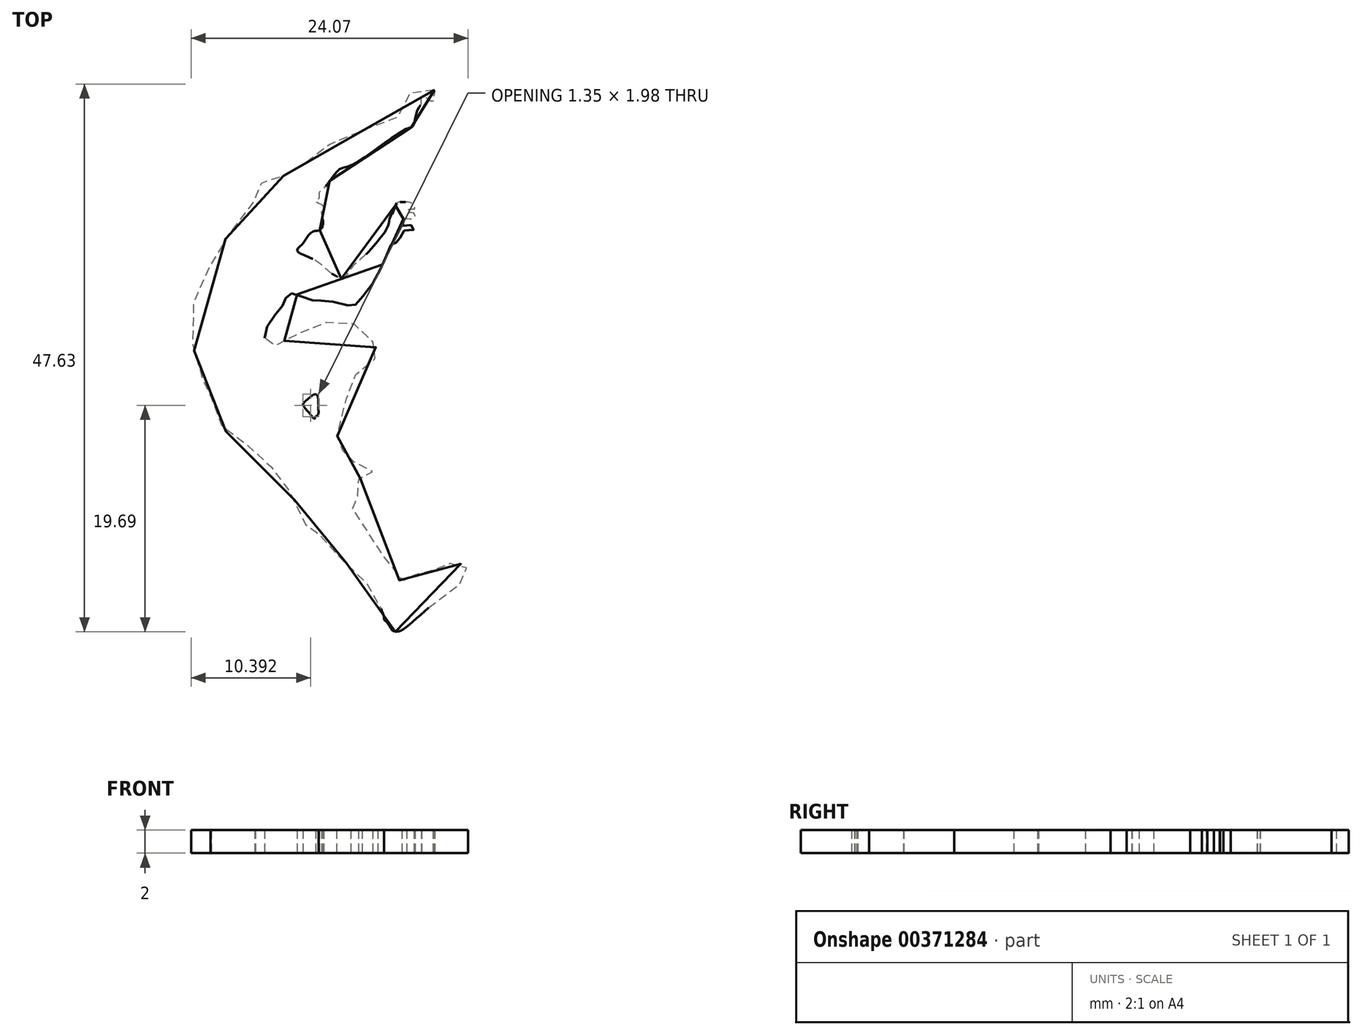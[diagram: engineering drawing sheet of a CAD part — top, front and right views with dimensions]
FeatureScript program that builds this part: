
annotation { "Feature Type Name" : "Feature", "Feature Type Description" : "" }
export const myFeature = defineFeature(function(context is Context, id is Id, definition is map)
    precondition{}
    {
        {
            var Q0;
            Q0=qCreatedBy(makeId("Top.planeOp"),FACE);
            var sketch = newSketch(context, id + "F0", { "sketchPlane" : qUnion([Q0])});
            skFitSpline(sketch, "E0", {"points": [v(-17.82, 62.19) * mm, v(-18.26, 62.6) * mm, v(-19.6, 62.47) * mm, v(-20.06, 61.56) * mm, v(-20.42, 60.89) * mm, v(-20.85, 59.9) * mm, v(-21.2, 59.78) * mm, v(-21.72, 59.64) * mm, v(-23.67, 58.82) * mm, v(-25.69, 58.05) * mm, v(-26.86, 57.47) * mm, v(-27.4, 57.23) * mm, v(-28.35, 56.34) * mm, v(-29.32, 55.6) * mm, v(-30.18, 55) * mm, v(-30.54, 55.02) * mm, v(-30.78, 54.76) * mm, v(-31.46, 54.78) * mm, v(-32.1, 54.54) * mm, v(-32.9, 54.04) * mm, v(-33.26, 53.31) * mm, v(-33.43, 52.83) * mm, v(-33.4, 52.47) * mm, v(-33.74, 52.4) * mm, v(-34.58, 51.13) * mm, v(-36.17, 48.94) * mm, v(-36.99, 47.42) * mm, v(-37.7, 46.25) * mm, v(-38.45, 44.66) * mm, v(-38.88, 43) * mm, v(-38.93, 40.93) * mm, v(-38.6, 39.18) * mm, v(-38.07, 37.76) * mm, v(-37.97, 36.9) * mm, v(-37.59, 35.98) * mm, v(-37.4, 35.64) * mm, v(-37.25, 35.62) * mm, v(-37.27, 34.95) * mm, v(-36.94, 34.06) * mm, v(-36.34, 33.02) * mm, v(-35.42, 31.97) * mm, v(-34.46, 31.46) * mm, v(-33.35, 30.88) * mm, v(-32.54, 29.83) * mm, v(-31.77, 29.18) * mm, v(-31.14, 28.14) * mm, v(-30.6, 27.52) * mm, v(-29.68, 25.9) * mm, v(-29.12, 24.6) * mm, v(-28.7, 24.06) * mm, v(-28.11, 24.03) * mm, v(-27.9, 24) * mm, v(-27.87, 23.7) * mm, v(-27.63, 23.17) * mm, v(-27.08, 22.45) * mm, v(-26.26, 21.75) * mm, v(-24.96, 20.55) * mm, v(-23.6, 19.18) * mm, v(-22.63, 17.95) * mm, v(-22.54, 17.3) * mm, v(-22.42, 16.94) * mm, v(-22.2, 16.34) * mm, v(-22.2, 16.12) * mm, v(-21.84, 15.76) * mm, v(-21.53, 15.26) * mm, v(-21.07, 15.06) * mm, v(-20.32, 15.42) * mm, v(-18.55, 16.96) * mm, v(-16.19, 18.8) * mm, v(-14.99, 19.78) * mm, v(-14.9, 20.16) * mm, v(-15.04, 20.62) * mm, v(-15.35, 20.9) * mm, v(-15.88, 21) * mm, v(-16.62, 20.93) * mm, v(-17.13, 20.55) * mm, v(-17.68, 20.47) * mm, v(-18.2, 20.23) * mm, v(-18.55, 19.94) * mm, v(-19.5, 20) * mm, v(-19.68, 19.75) * mm, v(-20.18, 19.78) * mm, v(-20.47, 19.56) * mm, v(-20.78, 19.49) * mm, v(-21.72, 20.81) * mm, v(-24.96, 25.81) * mm, v(-25.08, 26.03) * mm, v(-24.99, 26.22) * mm, v(-24.72, 26.56) * mm, v(-24.17, 27.42) * mm, v(-24.17, 27.9) * mm, v(-24.41, 28.34) * mm, v(-23.83, 28.4) * mm, v(-23.28, 28.55) * mm, v(-23.23, 29.13) * mm, v(-23.57, 29.47) * mm, v(-24.72, 29.8) * mm, v(-25.2, 30.14) * mm, v(-25.62, 30.4) * mm, v(-25.8, 30.8) * mm, v(-26.07, 30.88) * mm, v(-26.3, 31.33) * mm, v(-26.16, 32.75) * mm, v(-25.53, 35.2) * mm, v(-24.74, 37) * mm, v(-24.66, 37.4) * mm, v(-24.45, 37.68) * mm, v(-23.2, 38.64) * mm, v(-22.8, 39) * mm, v(-22.76, 39.36) * mm, v(-23.12, 40.2) * mm, v(-23.78, 41.25) * mm, v(-25.02, 41.88) * mm, v(-26.4, 41.99) * mm, v(-27.82, 41.83) * mm, v(-28.97, 41.3) * mm, v(-30.45, 40.57) * mm, v(-31.62, 39.97) * mm, v(-32.12, 39.8) * mm, v(-32.46, 40) * mm, v(-32.59, 40.71) * mm, v(-32.09, 42.08) * mm, v(-31.08, 43.34) * mm, v(-30.8, 43.95) * mm, v(-30.45, 44.44) * mm, v(-29.7, 44.37) * mm, v(-28.54, 43.9) * mm, v(-27.87, 43.86) * mm, v(-26.56, 43.74) * mm, v(-24.86, 43.4) * mm, v(-24.61, 43.6) * mm, v(-23.46, 44.94) * mm, v(-22.3, 47.07) * mm, v(-21.64, 48.56) * mm, v(-21.42, 48.92) * mm, v(-21.03, 48.92) * mm, v(-20.81, 49.28) * mm, v(-20.54, 49.91) * mm, v(-19.68, 49.99) * mm, v(-19.66, 50.33) * mm, v(-20.04, 50.4) * mm, v(-20.58, 50.38) * mm, v(-20.6, 50.89) * mm, v(-20.22, 51.01) * mm, v(-19.68, 51) * mm, v(-19.51, 51.21) * mm, v(-19.64, 51.46) * mm, v(-20.02, 51.52) * mm, v(-20.22, 51.52) * mm, v(-20.16, 51.71) * mm, v(-19.75, 51.82) * mm, v(-19.53, 51.84) * mm, v(-19.59, 52.08) * mm, v(-19.9, 52.38) * mm, v(-20.58, 52.44) * mm, v(-21.1, 52.33) * mm, v(-21.37, 51.66) * mm, v(-21.64, 51.2) * mm, v(-21.78, 50.6) * mm, v(-22.09, 49.9) * mm, v(-22.7, 49.1) * mm, v(-23.76, 47.9) * mm, v(-25.13, 46.58) * mm, v(-25.76, 45.75) * mm, v(-26.21, 45.92) * mm, v(-26.7, 46.19) * mm, v(-27.4, 46.76) * mm, v(-28.6, 47.6) * mm, v(-29.74, 48.2) * mm, v(-29.3, 48.8) * mm, v(-28.83, 49.46) * mm, v(-28.25, 49.93) * mm, v(-27.85, 49.95) * mm, v(-27.56, 50.3) * mm, v(-27.51, 50.87) * mm, v(-27.62, 51.5) * mm, v(-27.56, 51.68) * mm, v(-27.44, 51.84) * mm, v(-27.48, 52.07) * mm, v(-27.78, 52.28) * mm, v(-28.1, 52.45) * mm, v(-28.1, 52.57) * mm, v(-27.87, 52.68) * mm, v(-27.83, 53.24) * mm, v(-27.56, 53.52) * mm, v(-26.8, 54.43) * mm, v(-26.22, 55.16) * mm, v(-25.83, 55.39) * mm, v(-25, 55.66) * mm, v(-23.63, 56.52) * mm, v(-21.82, 57.8) * mm, v(-20.8, 58.47) * mm, v(-19.97, 58.9) * mm, v(-19.7, 59.02) * mm, v(-19.5, 59.6) * mm, v(-19.23, 60.57) * mm, v(-19.04, 60.82) * mm, v(-18.95, 61.3) * mm, v(-18.96, 61.53) * mm, v(-18.74, 61.62) * mm, v(-18.47, 61.45) * mm, v(-18.06, 61.22) * mm, v(-17.86, 61.31) * mm, v(-17.93, 61.54) * mm, v(-17.9, 61.63) * mm, v(-17.81, 61.85) * mm, v(-17.82, 62.19) * mm]});
            skFitSpline(sketch, "E1", {"points": [v(-28.16, 35.74) * mm, v(-28.72, 35.4) * mm, v(-29.15, 34.99) * mm, v(-29.26, 34.82) * mm, v(-28.97, 34.4) * mm, v(-28.6, 33.94) * mm, v(-28.25, 33.58) * mm, v(-28.16, 33.79) * mm, v(-27.96, 33.88) * mm, v(-27.92, 34.79) * mm, v(-27.98, 35.62) * mm, v(-28.16, 35.74) * mm]});
            skSolve(sketch);
        }
        {
            var Q0;
            Q0=qSketchRegion(id+"F0",true);
            extrude(context, id + "F1", {"entities" : qUnion([Q0]), "depth" : 2 * mm});
        }
    });
